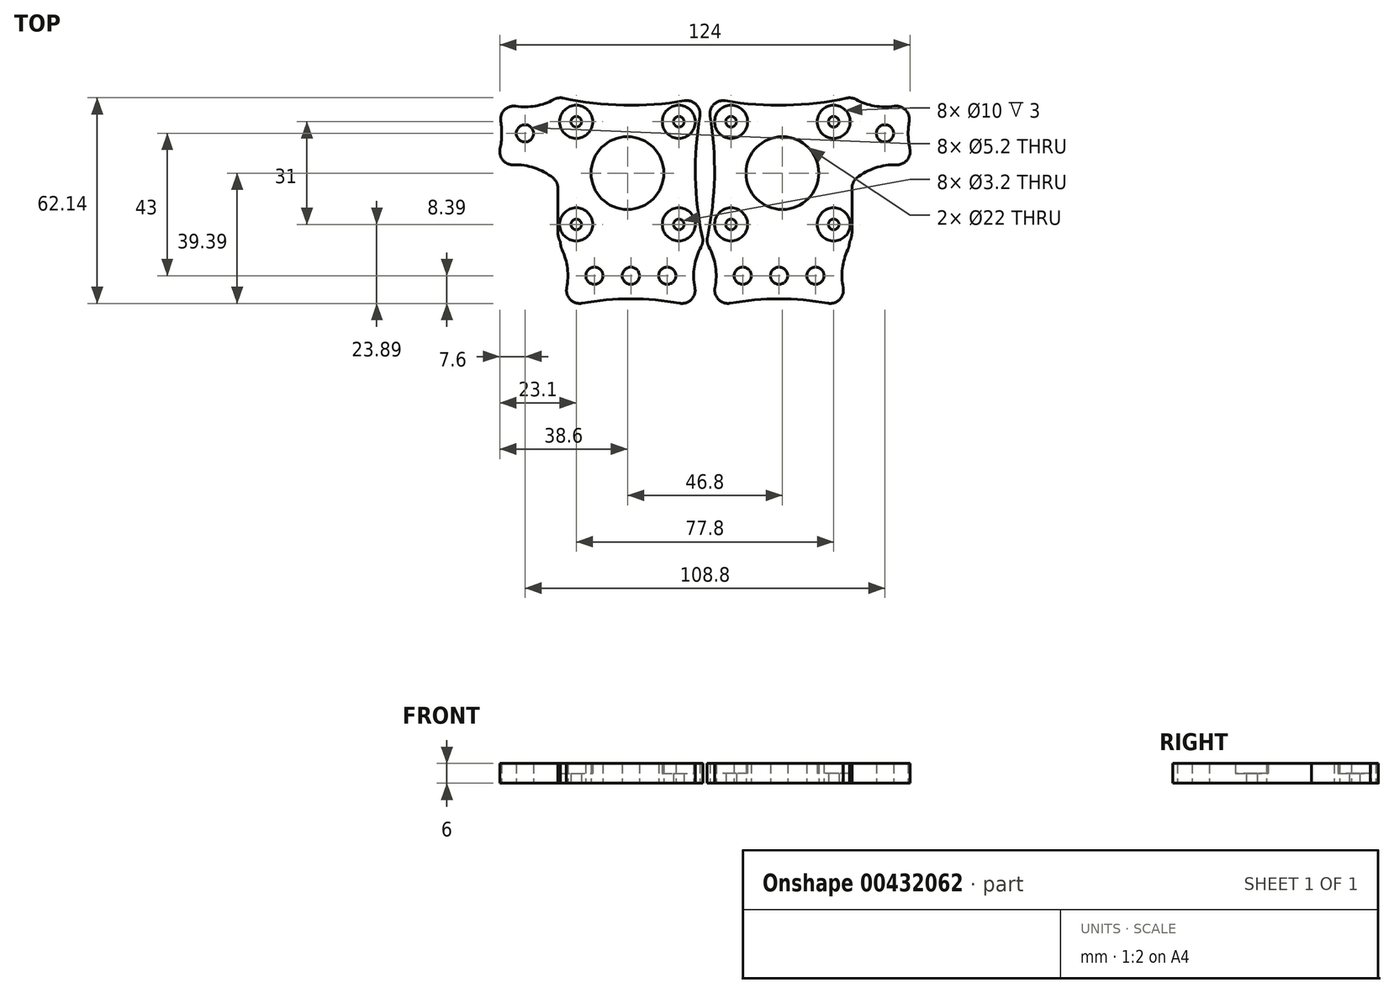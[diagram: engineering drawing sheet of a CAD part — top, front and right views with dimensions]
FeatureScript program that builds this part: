
annotation { "Feature Type Name" : "Feature", "Feature Type Description" : "" }
export const myFeature = defineFeature(function(context is Context, id is Id, definition is map)
    precondition{}
    {
        {
            var Q0;
            Q0=qCreatedBy(makeId("Top.planeOp"),FACE);
            var sketch = newSketch(context, id + "F0", { "sketchPlane" : qUnion([Q0])});
            skCircle(sketch, "E0", {"center": v(0, 0) * mm, "radius": 1.6 * mm});
            skCircle(sketch, "E1.0.1.0", {"center": v(0, 31) * mm, "radius": 1.6 * mm});
            skCircle(sketch, "E1.1.0.0", {"center": v(31, 0) * mm, "radius": 1.6 * mm});
            skCircle(sketch, "E1.1.1.0", {"center": v(31, 31) * mm, "radius": 1.6 * mm});
            skLineSegment(sketch, "E1.direction1", {"start": v(0, 0) * mm, "end": v(31, 0) * mm, "construction": true});
            skLineSegment(sketch, "E1.direction2", {"start": v(0, 0) * mm, "end": v(0, 31) * mm, "construction": true});
            skCircle(sketch, "E2", {"center": v(15.5, 15.5) * mm, "radius": 11 * mm});
            skPoint(sketch, "E2.centerSnap0", {"position": v(15.5, 0) * mm});
            skPoint(sketch, "E2.centerSnap1", {"position": v(0, 15.5) * mm});
            skLineSegment(sketch, "E3.bottom", {"start": v(-7.5, 38.5) * mm, "end": v(36.5, 38.5) * mm});
            skLineSegment(sketch, "E3.top", {"start": v(-7.5, -5.5) * mm, "end": v(36.5, -5.5) * mm});
            skLineSegment(sketch, "E3.left", {"start": v(-7.5, 38.5) * mm, "end": v(-7.5, -5.5) * mm});
            skLineSegment(sketch, "E3.right", {"start": v(36.5, 38.5) * mm, "end": v(36.5, -5.5) * mm});
            skLineSegment(sketch, "E4.top", {"start": v(-7.5, -25.5) * mm, "end": v(36.5, -25.5) * mm});
            skLineSegment(sketch, "E4.left", {"start": v(-7.5, -5.5) * mm, "end": v(-7.5, -25.5) * mm});
            skLineSegment(sketch, "E4.right", {"start": v(36.5, -5.5) * mm, "end": v(36.5, -25.5) * mm});
            skLineSegment(sketch, "E5.bottom", {"start": v(36.5, 38.5) * mm, "end": v(56.5, 38.5) * mm});
            skCircle(sketch, "E6", {"center": v(36.5, -5.5) * mm, "radius": 0.75 * mm});
            skPoint(sketch, "E7.centerSnap0", {"position": v(56.5, 16.5) * mm});
            skPoint(sketch, "E7.centerSnap1", {"position": v(46.5, 38.5) * mm});
            skCircle(sketch, "E8", {"center": v(46.5, 27.5) * mm, "radius": 2.6 * mm});
            skCircle(sketch, "E9", {"center": v(14.5, -15.5) * mm, "radius": 2.6 * mm});
            skPoint(sketch, "E9.centerSnap0", {"position": v(36.5, -15.5) * mm});
            skPoint(sketch, "E9.centerSnap1", {"position": v(14.5, -25.5) * mm});
            skCircle(sketch, "E10", {"center": v(25.5, -15.5) * mm, "radius": 2.6 * mm});
            skCircle(sketch, "E11", {"center": v(3.5, -15.5) * mm, "radius": 2.6 * mm});
            skArc(sketch, "E12", {"start": v(-7.5, 38.5) * mm, "mid": v(14.5, 36) * mm, "end": v(36.5, 38.5) * mm});
            skArc(sketch, "E13", {"start": v(-7.5, -5.5) * mm, "mid": v(-5, 16.5) * mm, "end": v(-7.5, 38.5) * mm});
            skArc(sketch, "E14", {"start": v(36.5, -25.5) * mm, "mid": v(14.5, -22.5) * mm, "end": v(-7.5, -25.5) * mm});
            skArc(sketch, "E15", {"start": v(36.5, 38.5) * mm, "mid": v(46.5, 35.5) * mm, "end": v(56.5, 38.5) * mm});
            skArc(sketch, "E16", {"start": v(36.5, -5.5) * mm, "mid": v(33.5, -15.5) * mm, "end": v(36.5, -25.5) * mm});
            skArc(sketch, "E17", {"start": v(-7.5, -25.5) * mm, "mid": v(-4.5, -15.5) * mm, "end": v(-7.5, -5.5) * mm});
            skCircle(sketch, "E18", {"center": v(0, 0) * mm, "radius": 5 * mm});
            skCircle(sketch, "E19.0.1.0", {"center": v(0, 31) * mm, "radius": 5 * mm});
            skCircle(sketch, "E19.1.0.0", {"center": v(31, 0) * mm, "radius": 5 * mm});
            skCircle(sketch, "E19.1.1.0", {"center": v(31, 31) * mm, "radius": 5 * mm});
            skLineSegment(sketch, "E20", {"start": v(36.5, 16.5) * mm, "end": v(56.5, 16.5) * mm});
            skLineSegment(sketch, "E21", {"start": v(56.5, 16.5) * mm, "end": v(56.5, 38.5) * mm});
            skArc(sketch, "E22", {"start": v(56.5, 38.5) * mm, "mid": v(53.5, 27.5) * mm, "end": v(56.5, 16.5) * mm});
            skArc(sketch, "E23", {"start": v(56.5, 16.5) * mm, "mid": v(45.9, 17.68) * mm, "end": v(36.5, 12.66) * mm});
            skSolve(sketch);
        }
        {
            var Q0;
            Q0=makeQuery(id+"F0.imprint","IMPRINT",FACE,{"disambiguationData":[TD([[makeQuery(id+"F0.imprint","IMPRINT",EDGE,{"derivedFrom":sQuery(id+"F0.wireOp",EDGE,"E7")}),-1.0]])]});
            var Q1;
            Q1=makeQuery(id+"F0.imprint","IMPRINT",FACE,{"disambiguationData":[TD([[makeQuery(id+"F0.imprint","IMPRINT",EDGE,{"derivedFrom":sQuery(id+"F0.wireOp",EDGE,"E9")}),-1.0]])]});
            var Q2;
            Q2=makeQuery(id+"F0.imprint","IMPRINT",FACE,{"disambiguationData":[TD([[makeQuery(id+"F0.imprint","IMPRINT",EDGE,{"derivedFrom":sQuery(id+"F0.wireOp",EDGE,"E2")}),-1.0]])]});
            var Q3;
            Q3=makeQuery(id+"F0.imprint","IMPRINT",FACE,{"disambiguationData":[TD([[makeQuery(id+"F0.imprint","IMPRINT",EDGE,{"derivedFrom":sQuery(id+"F0.wireOp",EDGE,"E8")}),-1.0]])]});
            var Q4;
            {var subQ0=sQuery(id+"F0.wireOp",EDGE,"E20");var subQ1=sQuery(id+"F0.wireOp",EDGE,"E3.right");var subQ2=makeQuery(id+"F0.imprint","INTERSECT",VERTEX,{"derivedFrom":[subQ1,subQ0]});Q4=makeQuery(id+"F0.imprint","IMPRINT",FACE,{"disambiguationData":[TD([[makeQuery(id+"F0.imprint","IMPRINT",EDGE,{"disambiguationData":[TD([[subQ2,-1.0]])],"derivedFrom":subQ1}),1.0]])]});}
            extrude(context, id + "F1", {"entities" : qUnion([Q0, Q1, Q2, Q3, Q4]), "depth" : 6 * mm});
        }
        {
            var Q0;
            Q0=makeQuery(id+"F1.opExtrude","SWEPT_EDGE",EDGE,{"disambiguationData":[OSD([sQuery(id+"F0.wireOp",EDGE,"E4.top"),sQuery(id+"F0.wireOp",EDGE,"E4.right"),sQuery(id+"F0.wireOp",EDGE,"E14")])]});
            var Q1;
            Q1=makeQuery(id+"F1.opExtrude","SWEPT_EDGE",EDGE,{"disambiguationData":[OSD([sQuery(id+"F0.wireOp",EDGE,"E4.top"),sQuery(id+"F0.wireOp",EDGE,"E4.left"),sQuery(id+"F0.wireOp",EDGE,"E14")])]});
            var Q2;
            Q2=makeQuery(id+"F1.opExtrude","SWEPT_EDGE",EDGE,{"disambiguationData":[OSD([sQuery(id+"F0.wireOp",EDGE,"E3.bottom"),sQuery(id+"F0.wireOp",EDGE,"E3.left"),sQuery(id+"F0.wireOp",EDGE,"E12"),sQuery(id+"F0.wireOp",EDGE,"E13")])]});
            var Q3;
            Q3=makeQuery(id+"F1.opExtrude","SWEPT_EDGE",EDGE,{"disambiguationData":[OSD([sQuery(id+"F0.wireOp",EDGE,"E5.bottom"),sQuery(id+"F0.wireOp",EDGE,"E5.right"),sQuery(id+"F0.wireOp",EDGE,"rQCq7UAb-19qp-IdM4-Piu0-ZXsqGDvIfrWA")])]});
            var Q4;
            Q4=makeQuery(id+"F1.opExtrude","SWEPT_EDGE",EDGE,{"disambiguationData":[OSD([sQuery(id+"F0.wireOp",EDGE,"E5.top"),sQuery(id+"F0.wireOp",EDGE,"E5.right"),sQuery(id+"F0.wireOp",EDGE,"rQCq7UAb-19qp-IdM4-Piu0-ZXsqGDvIfrWA")])]});
            var Q5;
            Q5=makeQuery(id+"F1.opExtrude","SWEPT_EDGE",EDGE,{"disambiguationData":[OSD([sQuery(id+"F0.wireOp",EDGE,"E3.bottom"),sQuery(id+"F0.wireOp",EDGE,"E5.bottom"),sQuery(id+"F0.wireOp",EDGE,"E3.right"),sQuery(id+"F0.wireOp",EDGE,"E12"),sQuery(id+"F0.wireOp",EDGE,"E15")])]});
            var Q6;
            Q6=makeQuery(id+"F1.opExtrude","SWEPT_EDGE",EDGE,{"disambiguationData":[OSD([sQuery(id+"F0.wireOp",EDGE,"E3.left"),sQuery(id+"F0.wireOp",EDGE,"E3.top"),sQuery(id+"F0.wireOp",EDGE,"E4.left"),sQuery(id+"F0.wireOp",EDGE,"E13"),sQuery(id+"F0.wireOp",EDGE,"E17")])]});
            var Q7;
            Q7=makeQuery(id+"F1.opExtrude","SWEPT_EDGE",EDGE,{"disambiguationData":[OSD([sQuery(id+"F0.wireOp",EDGE,"E20"),sQuery(id+"F0.wireOp",EDGE,"E21"),sQuery(id+"F0.wireOp",EDGE,"E22"),sQuery(id+"F0.wireOp",EDGE,"E23")])]});
            var Q8;
            Q8=makeQuery(id+"F1.opExtrude","SWEPT_EDGE",EDGE,{"disambiguationData":[OSD([sQuery(id+"F0.wireOp",EDGE,"E3.right"),sQuery(id+"F0.wireOp",EDGE,"E23")])]});
            fillet(context, id + "F2", {"entities" : qUnion([Q0, Q1, Q2, Q3, Q4, Q5, Q6, Q7, Q8]), "radius" : 4 * mm, "tangentPropagation" : true, "allowEdgeOverflow" : false});
        }
        {
            var Q0;
            Q0=makeQuery(id+"F1.opExtrude","SWEPT_EDGE",EDGE,{"disambiguationData":[OSD([sQuery(id+"F0.wireOp",EDGE,"E5.top"),sQuery(id+"F0.wireOp",EDGE,"E6")])]});
            var Q1;
            Q1=makeQuery(id+"F1.opExtrude","SWEPT_EDGE",EDGE,{"disambiguationData":[OSD([sQuery(id+"F0.wireOp",EDGE,"E4.right"),sQuery(id+"F0.wireOp",EDGE,"E6")])]});
            fillet(context, id + "F3", {"entities" : qUnion([Q0, Q1]), "radius" : 5 * mm, "tangentPropagation" : true, "allowEdgeOverflow" : false});
        }
        {
            var Q0;
            Q0=makeQuery(id+"F0.imprint","IMPRINT",FACE,{"disambiguationData":[TD([[makeQuery(id+"F0.imprint","IMPRINT",EDGE,{"derivedFrom":sQuery(id+"F0.wireOp",EDGE,"E1.0.1.0")}),-1.0]])]});
            var Q1;
            Q1=makeQuery(id+"F0.imprint","IMPRINT",FACE,{"disambiguationData":[TD([[makeQuery(id+"F0.imprint","IMPRINT",EDGE,{"derivedFrom":sQuery(id+"F0.wireOp",EDGE,"E1.1.1.0")}),-1.0]])]});
            var Q2;
            Q2=makeQuery(id+"F0.imprint","IMPRINT",FACE,{"disambiguationData":[TD([[makeQuery(id+"F0.imprint","IMPRINT",EDGE,{"derivedFrom":sQuery(id+"F0.wireOp",EDGE,"E0")}),-1.0]])]});
            var Q3;
            Q3=makeQuery(id+"F0.imprint","IMPRINT",FACE,{"disambiguationData":[TD([[makeQuery(id+"F0.imprint","IMPRINT",EDGE,{"derivedFrom":sQuery(id+"F0.wireOp",EDGE,"E1.1.0.0")}),-1.0]])]});
            extrude(context, id + "F4", {"entities" : qUnion([Q0, Q1, Q2, Q3]), "operationType" : NewBodyOperationType.ADD, "depth" : 3 * mm});
        }
        {
            var Q0;
            Q0=makeQuery(id+"F1.opExtrude","SWEPT_BODY",BODY,{"disambiguationData":[OSD([sQuery(id+"F0.wireOp",EDGE,"E2"),sQuery(id+"F0.wireOp",EDGE,"E6"),sQuery(id+"F0.wireOp",EDGE,"E7"),sQuery(id+"F0.wireOp",EDGE,"E8"),sQuery(id+"F0.wireOp",EDGE,"DGOVMgoc-u9ZP-N8C2-JEQD-QCCm1VvnKdqT"),sQuery(id+"F0.wireOp",EDGE,"E9"),sQuery(id+"F0.wireOp",EDGE,"E10"),sQuery(id+"F0.wireOp",EDGE,"E11"),sQuery(id+"F0.wireOp",EDGE,"E12"),sQuery(id+"F0.wireOp",EDGE,"E13"),sQuery(id+"F0.wireOp",EDGE,"rQCq7UAb-19qp-IdM4-Piu0-ZXsqGDvIfrWA"),sQuery(id+"F0.wireOp",EDGE,"E14"),sQuery(id+"F0.wireOp",EDGE,"rVSBWCbp-ZJMo-doA0-Zq5G-kSpUdmJG42N7"),sQuery(id+"F0.wireOp",EDGE,"E15"),sQuery(id+"F0.wireOp",EDGE,"E16"),sQuery(id+"F0.wireOp",EDGE,"E17"),sQuery(id+"F0.wireOp",EDGE,"E18"),sQuery(id+"F0.wireOp",EDGE,"E19.0.1.0"),sQuery(id+"F0.wireOp",EDGE,"E19.1.0.0"),sQuery(id+"F0.wireOp",EDGE,"E19.1.1.0")])]});
            var Q1;
            Q1=qCreatedBy(makeId("Right.planeOp"),FACE);
            mirror(context, id + "F5", {"entities" : qUnion([Q0]), "mirrorPlane" : qUnion([Q1])});
        }
        {
            var Q0;
            Q0=makeQuery(id+"F5.opPattern","COPY",BODY,{"derivedFrom":makeQuery(id+"F1.opExtrude","SWEPT_BODY",BODY,{"disambiguationData":[OSD([sQuery(id+"F0.wireOp",EDGE,"E2"),sQuery(id+"F0.wireOp",EDGE,"E6"),sQuery(id+"F0.wireOp",EDGE,"E7"),sQuery(id+"F0.wireOp",EDGE,"E8"),sQuery(id+"F0.wireOp",EDGE,"DGOVMgoc-u9ZP-N8C2-JEQD-QCCm1VvnKdqT"),sQuery(id+"F0.wireOp",EDGE,"E9"),sQuery(id+"F0.wireOp",EDGE,"E10"),sQuery(id+"F0.wireOp",EDGE,"E11"),sQuery(id+"F0.wireOp",EDGE,"E12"),sQuery(id+"F0.wireOp",EDGE,"E13"),sQuery(id+"F0.wireOp",EDGE,"rQCq7UAb-19qp-IdM4-Piu0-ZXsqGDvIfrWA"),sQuery(id+"F0.wireOp",EDGE,"E14"),sQuery(id+"F0.wireOp",EDGE,"rVSBWCbp-ZJMo-doA0-Zq5G-kSpUdmJG42N7"),sQuery(id+"F0.wireOp",EDGE,"E15"),sQuery(id+"F0.wireOp",EDGE,"E16"),sQuery(id+"F0.wireOp",EDGE,"E17"),sQuery(id+"F0.wireOp",EDGE,"E18"),sQuery(id+"F0.wireOp",EDGE,"E19.0.1.0"),sQuery(id+"F0.wireOp",EDGE,"E19.1.0.0"),sQuery(id+"F0.wireOp",EDGE,"E19.1.1.0")])]}),"instanceName":"1"});
            transform(context, id + "F6", {"entities" : qUnion([Q0]), "transformType" : TransformType.TRANSLATION_3D, "dx" : -15.8 * mm, "dy" : 0 * mm, "dz" : 0 * mm, "makeCopy" : false});
        }
    });
